# Revit family: Comfort_Window_D_Top_Hung_Standard
name_source: partatom
category: Windows
revit_build: Autodesk Revit 2014 (Build: 20130308_1515(x64)
units: mm (PartAtom-declared; Revit-internal decimal feet)

## types (4) — shared parameters
DG Gasket Thickness = 12 mm  [stored 0.0393701 ft]
Description = Comfort Window, Top Hung, Type D
Double Glazing Gasket Finish = Double Glazing Gasket Material
Frame Depth = 33 mm
Frame Edge Thickness = 26 mm
Limit Fixed Pane Height Max = 1800 mm
Limit Fixed Pane Height Min = 200 mm
Limit Fixed Pane Width Max = 1800 mm
Limit Fixed Pane Width Min = 200 mm
Limit Sash Height Max = 1200 mm
Limit Sash Height Min = 300 mm  [stored 0.984252 ft]
Limit Sash Width Max = 1200 mm
Limit Sash Width Min = 300 mm  [stored 0.984252 ft]
Limit Window Width Max = 1275 mm
Limit Window Width Min = 375 mm
Manufacturer = Crealco
Max System DG One Piece Thickness = 4 mm  [stored 0.0131234 ft]
Max System DG Unit Thickness = 20 mm  [stored 0.0656168 ft]
Model = Comfort Window
Rough Height = 1647 mm
Rough Width = 2226 mm
Sash Frame Gap = 5 mm  [stored 0.0164042 ft]
Sash Frame Side Gap = 12 mm  [stored 0.0393701 ft]
Sash Side Gap = 38 mm
Set Sash Height = 515 mm
Transom Height = 27 mm  [stored 0.0885827 ft]
URL = http://www.crealco.co.za
zero-valued in all types: Visual Light Transmittance

## per-type parameters (varying)
| type | Clearvue SHGC Value | Clearvue U Value | Energy Advantage SHGC Value | Energy Advantage U Value | Intruderprufe LowE SHGC Value | Intruderprufe LowE U Value | Intruderprufe SHGC Value | Intruderprufe U Value | SmartGlass Elite SHGC Value | SmartGlass Elite U Value | SmartGlass Plus SHGC Value | SmartGlass Plus U Value | SmartGlass Standard SHGC Value | SmartGlass Standard U Value | SmartGlass Superior SHGC Value | SmartGlass Superior U Value | Window Height | Window Width |
| Comfort-0609T | 0.505 | 6.15 | 0.454 | 5 | 0.433 | 4.87 | 0.482 | 6.06 | 0.253 | 3.88 | 0.341 | 4 | 0.454 | 4.42 | 0.222 | 3.89 | 890 mm  [stored 2.91995 ft] | 590 mm |
| Comfort-0612T | 0.505 | 6.15 | 0.454 | 5 | 0.433 | 4.87 | 0.482 | 6.06 | 0.253 | 3.88 | 0.341 | 4 | 0.454 | 4.42 | 0.22 | 3.89 | 1190 mm  [stored 3.9042 ft] | 590 mm |
| Comfort-0909T | 0.552 | 6.12 | 0.495 | 4.83 | 0.471 | 4.71 | 0.526 | 6.02 | 0.273 | 3.6 | 0.37 | 3.73 | 0.494 | 4.21 | 0.239 | 3.61 | 890 mm  [stored 2.91995 ft] | 890 mm  [stored 2.91995 ft] |
| Comfort-0912T | 0.605 | 6.07 | 0.542 | 4.63 | 0.513 | 4.51 | 0.575 | 5.97 | 0.296 | 3.26 | 0.402 | 3.41 | 0.539 | 3.95 | 0.258 | 3.26 | 1190 mm  [stored 3.9042 ft] | 890 mm  [stored 2.91995 ft] |

note: [stored X ft] marks values corroborated as IEEE doubles in the binary element streams (Revit-internal decimal feet)

## geometry (parser evidence)
native form markers: Sweep x23
no freeform markers — native parametric forms only
